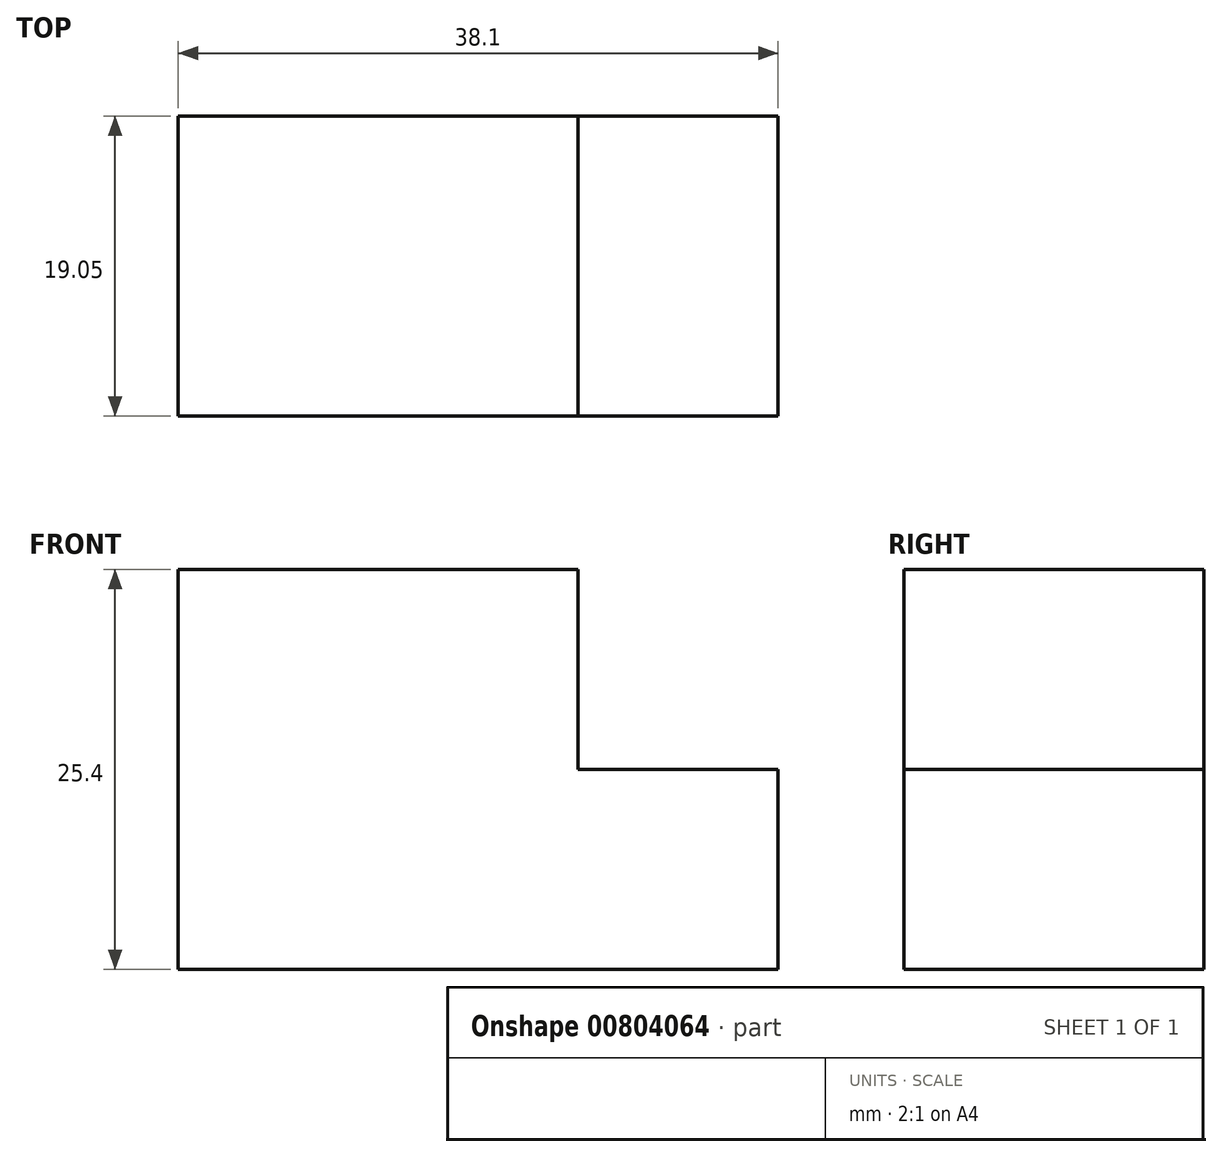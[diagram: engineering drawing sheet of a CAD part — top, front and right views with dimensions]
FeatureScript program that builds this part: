
annotation { "Feature Type Name" : "Feature", "Feature Type Description" : "" }
export const myFeature = defineFeature(function(context is Context, id is Id, definition is map)
    precondition{}
    {
        {
            var Q0;
            Q0=qCreatedBy(makeId("Front.planeOp"),FACE);
            var sketch = newSketch(context, id + "F0", { "sketchPlane" : qUnion([Q0])});
            skLineSegment(sketch, "E0", {"start": v(0, 0) * mm, "end": v(38.1, 0) * mm});
            skLineSegment(sketch, "E1", {"start": v(38.1, 0) * mm, "end": v(38.1, 12.7) * mm});
            skLineSegment(sketch, "E2", {"start": v(38.1, 12.7) * mm, "end": v(25.4, 12.7) * mm});
            skLineSegment(sketch, "E3", {"start": v(25.4, 12.7) * mm, "end": v(25.4, 25.4) * mm});
            skLineSegment(sketch, "E4", {"start": v(25.4, 25.4) * mm, "end": v(0, 25.4) * mm});
            skLineSegment(sketch, "E5", {"start": v(0, 25.4) * mm, "end": v(0, 0) * mm});
            skSolve(sketch);
        }
        {
            var Q0;
            Q0=makeQuery(id+"F0.imprint","IMPRINT",FACE,{"disambiguationData":[TD([[makeQuery(id+"F0.imprint","IMPRINT",EDGE,{"derivedFrom":sQuery(id+"F0.wireOp",EDGE,"E0")}),1.0]])]});
            extrude(context, id + "F1", {"entities" : qUnion([Q0]), "depth" : 19.05 * mm, "offsetDistance" : 25.4 * mm});
        }
    });
